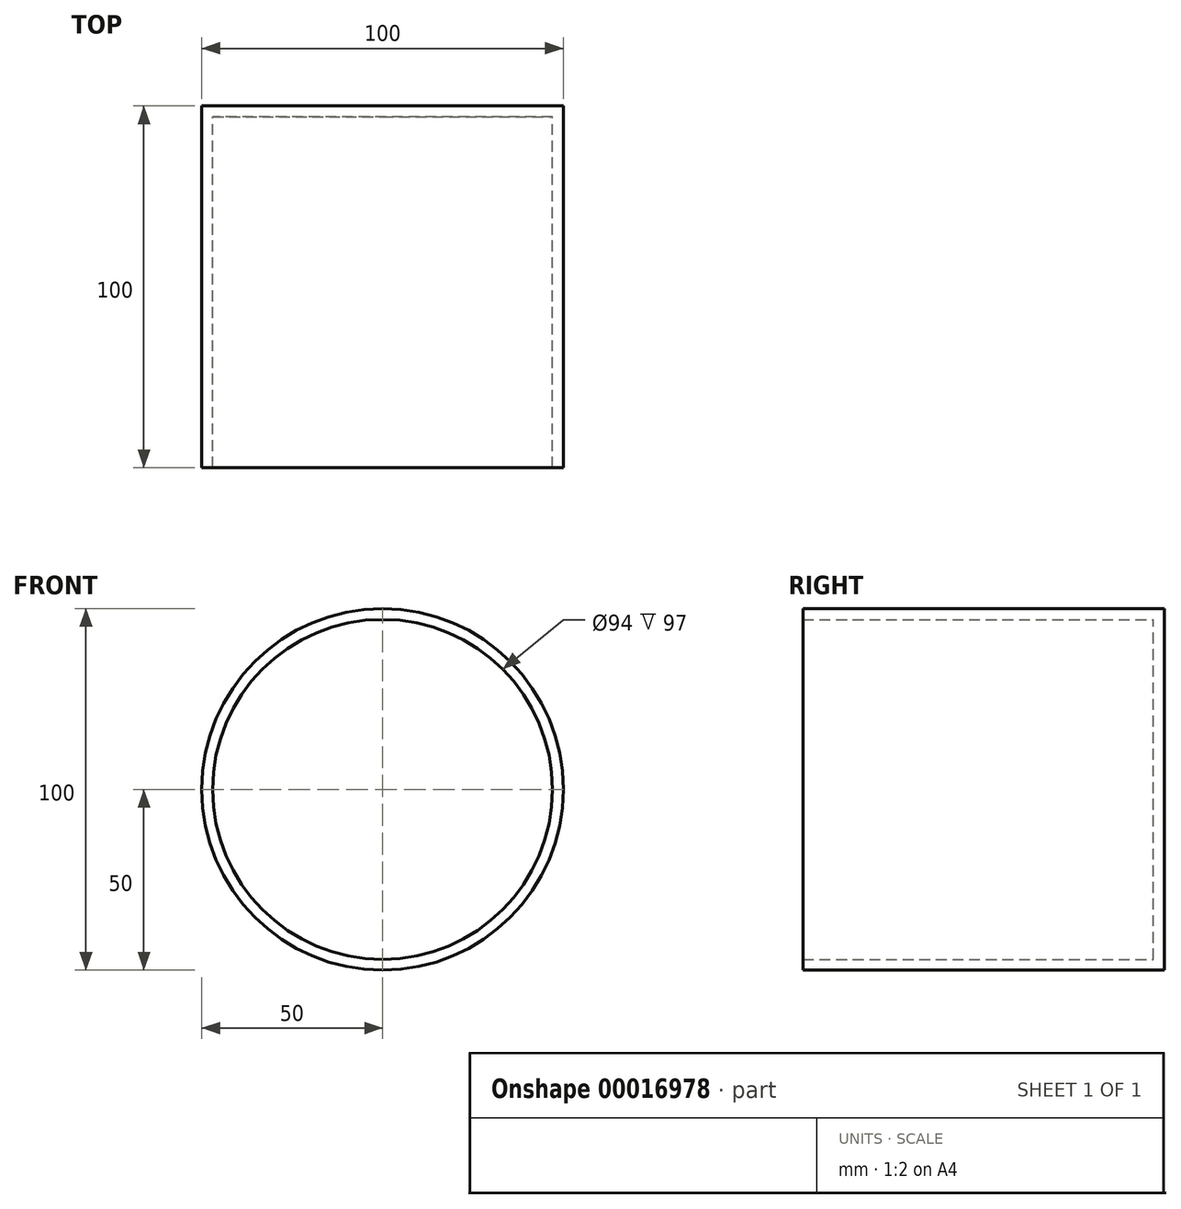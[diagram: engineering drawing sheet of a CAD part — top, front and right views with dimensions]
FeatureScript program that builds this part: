
annotation { "Feature Type Name" : "Feature", "Feature Type Description" : "" }
export const myFeature = defineFeature(function(context is Context, id is Id, definition is map)
    precondition{}
    {
        {
            var Q0;
            Q0=qCreatedBy(makeId("Front.planeOp"),FACE);
            var sketch = newSketch(context, id + "F0", { "sketchPlane" : qUnion([Q0])});
            skCircle(sketch, "E0", {"center": v(0, 0) * mm, "radius": 50 * mm});
            skSolve(sketch);
        }
        {
            var Q0;
            Q0 = qSketchRegion(id + "F0", true);
            extrude(context, id + "F1", {"entities" : qUnion([Q0]), "depth" : 100 * mm});
        }
        {
            var Q0;
            Q0=makeQuery(id+"F1.opExtrude","CAP_FACE",FACE,{"disambiguationData":[OSD([sQuery(id+"F0.wireOp",EDGE,"E0")])],"isStart":false});
            shell(context, id + "F2", {"entities" : qUnion([Q0]), "thickness" : 3 * mm});
        }
    });
